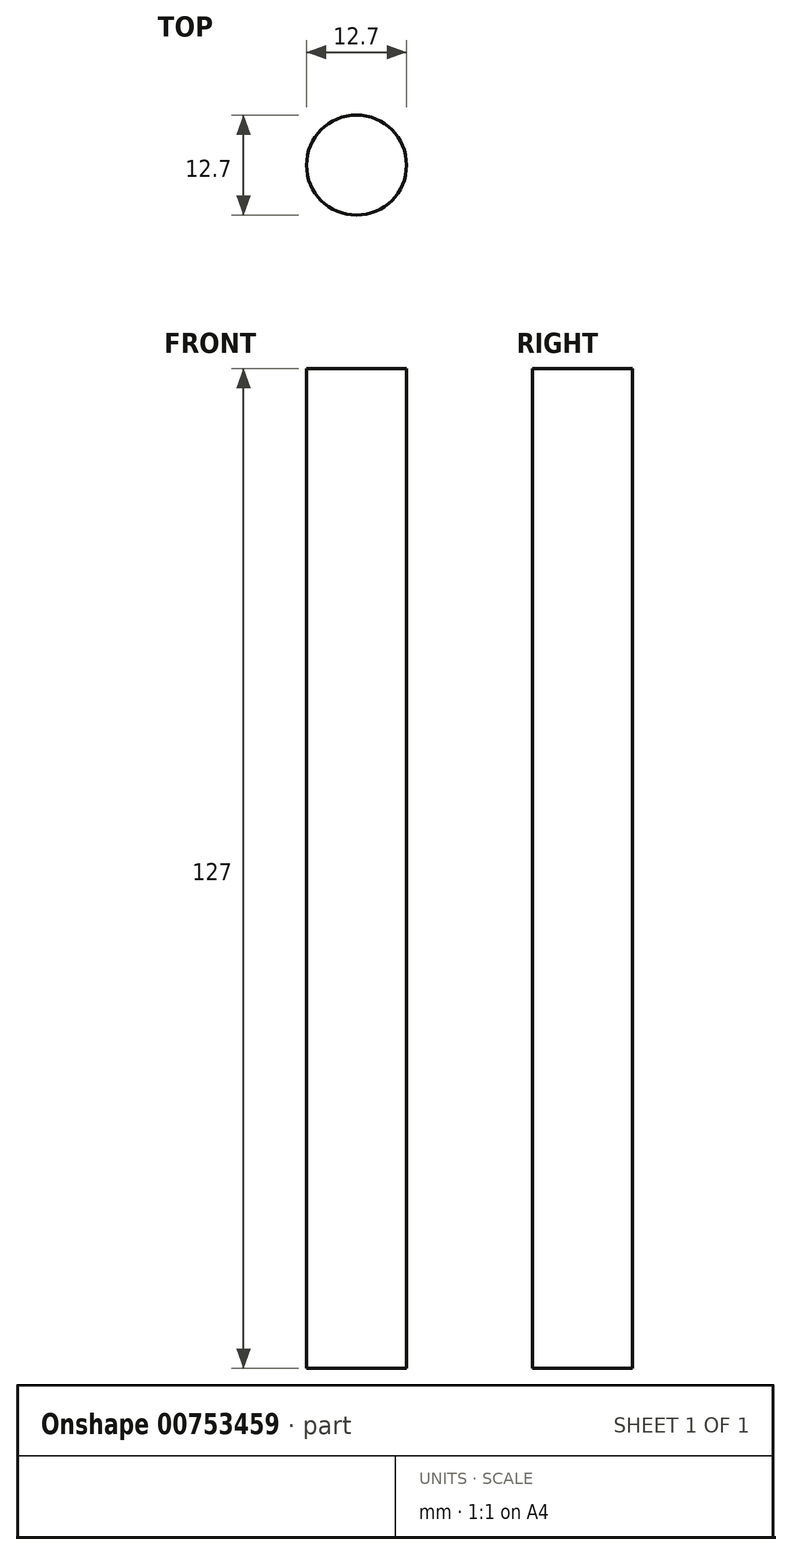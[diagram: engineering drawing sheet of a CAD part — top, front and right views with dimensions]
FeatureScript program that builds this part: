
annotation { "Feature Type Name" : "Feature", "Feature Type Description" : "" }
export const myFeature = defineFeature(function(context is Context, id is Id, definition is map)
    precondition{}
    {
        {
            var Q0;
            Q0=qCreatedBy(makeId("Top.planeOp"),FACE);
            var sketch = newSketch(context, id + "F0", { "sketchPlane" : qUnion([Q0])});
            skCircle(sketch, "E0", {"center": v(0, 0) * mm, "radius": 6.35 * mm});
            skSolve(sketch);
        }
        {
            var Q0;
            Q0=makeQuery(id+"F0.imprint","IMPRINT",FACE,{"disambiguationData":[TD([[makeQuery(id+"F0.imprint","IMPRINT",EDGE,{"derivedFrom":sQuery(id+"F0.wireOp",EDGE,"E0")}),1.0]])]});
            extrude(context, id + "F1", {"entities" : qUnion([Q0]), "depth" : 127 * mm, "offsetDistance" : 25.4 * mm});
        }
    });
